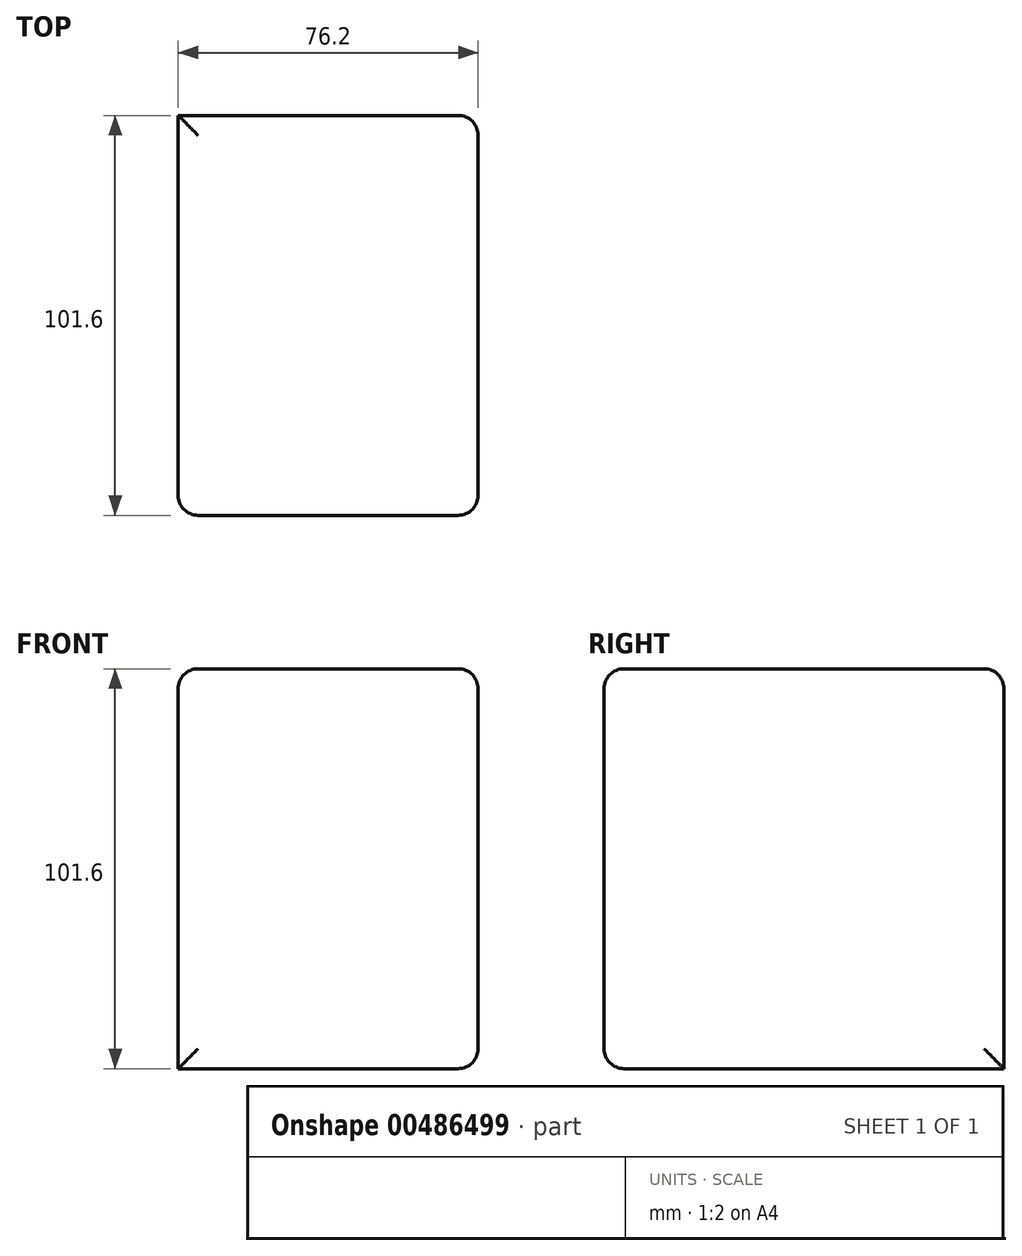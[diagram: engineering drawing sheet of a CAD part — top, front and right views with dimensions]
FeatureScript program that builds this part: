
annotation { "Feature Type Name" : "Feature", "Feature Type Description" : "" }
export const myFeature = defineFeature(function(context is Context, id is Id, definition is map)
    precondition{}
    {
        {
            var Q0;
            Q0=qCreatedBy(makeId("Front.planeOp"),FACE);
            var sketch = newSketch(context, id + "F0", { "sketchPlane" : qUnion([Q0])});
            skLineSegment(sketch, "E0.bottom", {"start": v(0, 0) * mm, "end": v(76.2, 0) * mm});
            skLineSegment(sketch, "E0.top", {"start": v(0, 101.6) * mm, "end": v(76.2, 101.6) * mm});
            skLineSegment(sketch, "E0.left", {"start": v(0, 0) * mm, "end": v(0, 101.6) * mm});
            skLineSegment(sketch, "E0.right", {"start": v(76.2, 0) * mm, "end": v(76.2, 101.6) * mm});
            skSolve(sketch);
        }
        {
            var Q0;
            Q0=makeQuery(id+"F0.imprint","IMPRINT",FACE,{"disambiguationData":[TD([[makeQuery(id+"F0.imprint","IMPRINT",EDGE,{"derivedFrom":sQuery(id+"F0.wireOp",EDGE,"E0.bottom")}),1.0]])]});
            extrude(context, id + "F1", {"entities" : qUnion([Q0]), "depth" : 101.6 * mm});
        }
        {
            var Q0;
            Q0=makeQuery(id+"F1.opExtrude","CAP_EDGE",EDGE,{"disambiguationData":[OSD([sQuery(id+"F0.wireOp",EDGE,"E0.top")])],"isStart":false});
            var Q1;
            Q1=makeQuery(id+"F1.opExtrude","SWEPT_EDGE",EDGE,{"disambiguationData":[OSD([sQuery(id+"F0.wireOp",EDGE,"E0.top"),sQuery(id+"F0.wireOp",EDGE,"E0.left")])]});
            var Q2;
            Q2=makeQuery(id+"F1.opExtrude","SWEPT_EDGE",EDGE,{"disambiguationData":[OSD([sQuery(id+"F0.wireOp",EDGE,"E0.top"),sQuery(id+"F0.wireOp",EDGE,"E0.right")])]});
            var Q3;
            Q3=makeQuery(id+"F1.opExtrude","CAP_EDGE",EDGE,{"disambiguationData":[OSD([sQuery(id+"F0.wireOp",EDGE,"E0.right")])],"isStart":false});
            var Q4;
            Q4=makeQuery(id+"F1.opExtrude","CAP_EDGE",EDGE,{"disambiguationData":[OSD([sQuery(id+"F0.wireOp",EDGE,"E0.left")])],"isStart":false});
            var Q5;
            Q5=makeQuery(id+"F1.opExtrude","CAP_EDGE",EDGE,{"disambiguationData":[OSD([sQuery(id+"F0.wireOp",EDGE,"E0.bottom")])],"isStart":false});
            var Q6;
            Q6=makeQuery(id+"F1.opExtrude","SWEPT_EDGE",EDGE,{"disambiguationData":[OSD([sQuery(id+"F0.wireOp",EDGE,"E0.bottom"),sQuery(id+"F0.wireOp",EDGE,"E0.right")])]});
            var Q7;
            Q7=makeQuery(id+"F1.opExtrude","SWEPT_FACE",FACE,{"disambiguationData":[OSD([sQuery(id+"F0.wireOp",EDGE,"E0.right")])]});
            var Q8;
            Q8=makeQuery(id+"F1.opExtrude","CAP_EDGE",EDGE,{"disambiguationData":[OSD([sQuery(id+"F0.wireOp",EDGE,"E0.top")])],"isStart":true});
            fillet(context, id + "F2", {"entities" : qUnion([Q0, Q1, Q2, Q3, Q4, Q5, Q6, Q7, Q8]), "radius" : 5.08 * mm, "tangentPropagation" : true, "allowEdgeOverflow" : false});
        }
        {
            var Q0;
            Q0=makeQuery(id+"F1.opExtrude","SWEPT_FACE",FACE,{"disambiguationData":[OSD([sQuery(id+"F0.wireOp",EDGE,"E0.right")])]});
            var sketch = newSketch(context, id + "F3", { "sketchPlane" : qUnion([Q0])});
            skCircle(sketch, "E1", {"center": v(-50.8, 51.4) * mm, "radius": 29.1 * mm});
            skSolve(sketch);
        }
        {
            var Q0;
            Q0 = qSketchRegion(id + "F3", true);
            extrude(context, id + "F4", {"entities" : qUnion([Q0]), "operationType" : NewBodyOperationType.ADD, "oppositeDirection" : true, "depth" : 76.2 * mm});
        }
    });
